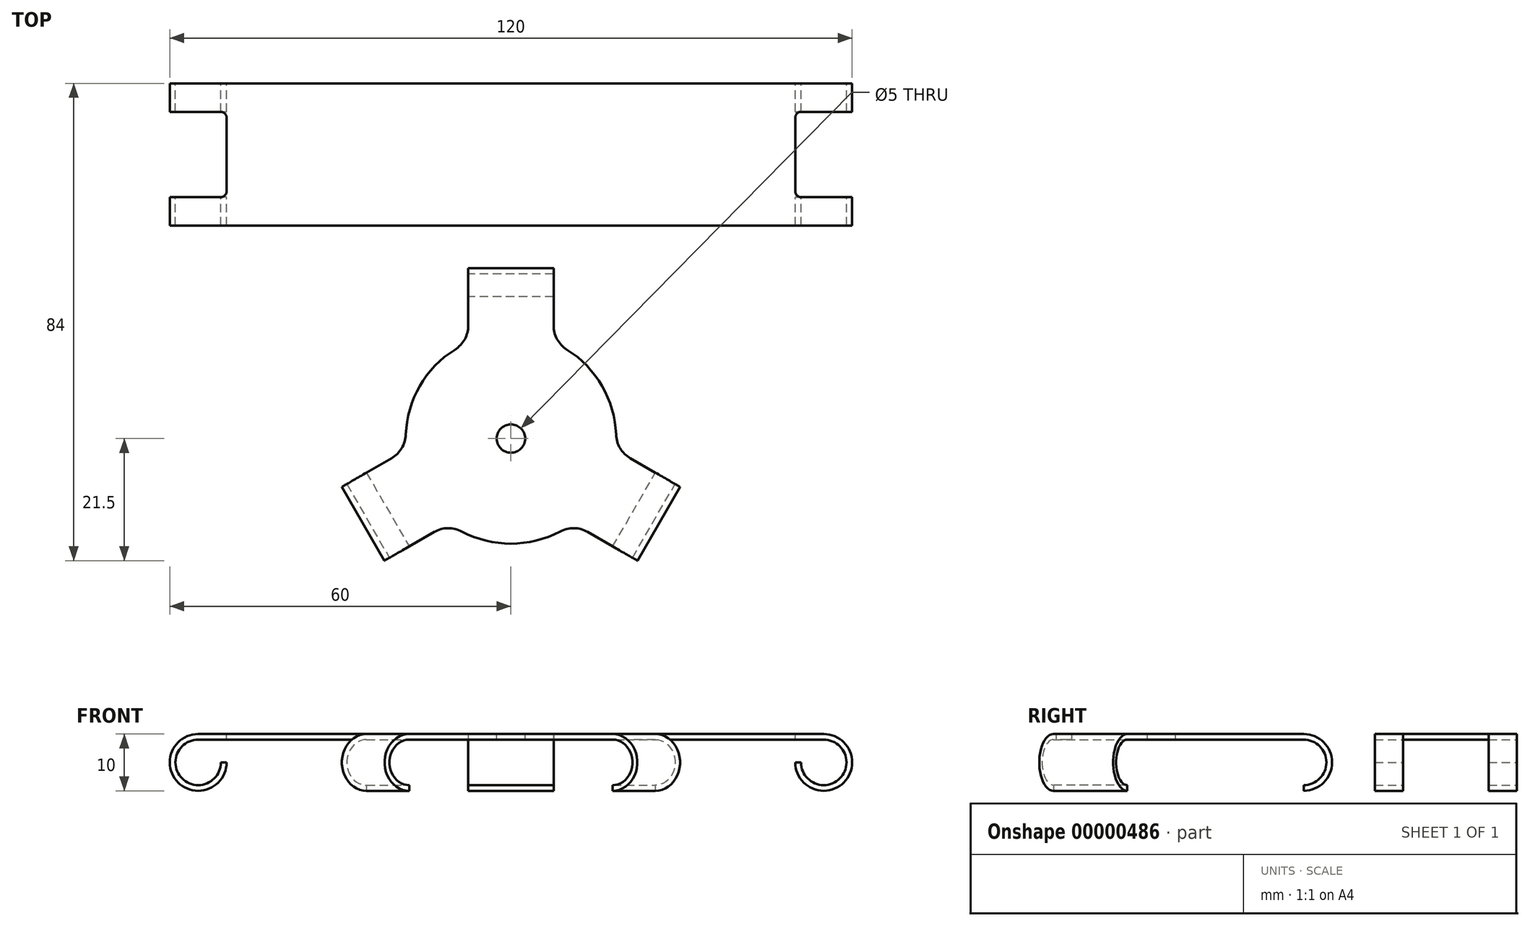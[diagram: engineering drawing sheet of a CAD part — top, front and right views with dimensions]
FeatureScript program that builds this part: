
annotation { "Feature Type Name" : "Feature", "Feature Type Description" : "" }
export const myFeature = defineFeature(function(context is Context, id is Id, definition is map)
    precondition{}
    {
        {
            var Q0;
            Q0     = qCreatedBy(makeId("Front.planeOp"), FACE);
            var sketch = newSketch(context, id + "F0", { "sketchPlane" : qUnion([Q0])});
            skLineSegment(sketch, "E0", {"start": v(-55, 0) * mm, "end": v(55, 0) * mm});
            skArc(sketch, "E1", {"start": v(-55, 0) * mm, "mid": v(-58.54, -8.54) * mm, "end": v(-50, -5) * mm});
            skArc(sketch, "E2", {"start": v(55, 0) * mm, "mid": v(58.54, -8.54) * mm, "end": v(50, -5) * mm});
            skArc(sketch, "E3.0", {"start": v(55, -1) * mm, "mid": v(57.83, -7.83) * mm, "end": v(51, -5) * mm});
            skLineSegment(sketch, "E3.1", {"start": v(-55, -1) * mm, "end": v(55, -1) * mm});
            skArc(sketch, "E3.2", {"start": v(-55, -1) * mm, "mid": v(-57.83, -7.83) * mm, "end": v(-51, -5) * mm});
            skLineSegment(sketch, "E4", {"start": v(-51, -5) * mm, "end": v(-50, -5) * mm});
            skLineSegment(sketch, "E5", {"start": v(51, -5) * mm, "end": v(50, -5) * mm});
            skSolve(sketch);
        }
        {
            var Q0;
            Q0=makeQuery(id+"F0.imprint","IMPRINT",FACE,{"disambiguationData":[TD([[makeQuery(id+"F0.imprint","IMPRINT",EDGE,{"derivedFrom":sQuery(id+"F0.wireOp",EDGE,"E0")}),-1.0]])]});
            extrude(context, id + "F1", {"entities" : qUnion([Q0]), "depth" : 25 * mm, "symmetric" : true});
        }
        {
            var Q0;
            Q0     = qCreatedBy(makeId("Top.planeOp"), FACE);
            var sketch = newSketch(context, id + "F2", { "sketchPlane" : qUnion([Q0])});
            skCircle(sketch, "E6", {"center": v(0, -50) * mm, "radius": 18.5 * mm});
            skLineSegment(sketch, "E7", {"start": v(0, -50) * mm, "end": v(0, -20) * mm, "construction": true});
            skLineSegment(sketch, "E8", {"start": v(0, -50) * mm, "end": v(25.98, -65) * mm, "construction": true});
            skLineSegment(sketch, "E9", {"start": v(0, -50) * mm, "end": v(-25.98, -65) * mm, "construction": true});
            skCircle(sketch, "E10", {"center": v(0, -50) * mm, "radius": 30 * mm, "construction": true});
            skLineSegment(sketch, "E11", {"start": v(-7.5, -20) * mm, "end": v(7.5, -20) * mm});
            skLineSegment(sketch, "E12", {"start": v(7.5, -20) * mm, "end": v(7.5, -45.67) * mm});
            skLineSegment(sketch, "E13", {"start": v(-7.5, -20) * mm, "end": v(-7.5, -45.67) * mm});
            skLineSegment(sketch, "E14", {"start": v(29.73, -58.5) * mm, "end": v(22.23, -71.5) * mm});
            skLineSegment(sketch, "E15", {"start": v(22.23, -71.5) * mm, "end": v(0, -58.66) * mm});
            skLineSegment(sketch, "E16", {"start": v(29.73, -58.5) * mm, "end": v(7.5, -45.67) * mm});
            skLineSegment(sketch, "E17", {"start": v(-29.73, -58.5) * mm, "end": v(-22.23, -71.5) * mm});
            skLineSegment(sketch, "E18", {"start": v(-22.23, -71.5) * mm, "end": v(0, -58.66) * mm});
            skLineSegment(sketch, "E19", {"start": v(-29.73, -58.5) * mm, "end": v(-7.5, -45.67) * mm});
            skSolve(sketch);
        }
        {
            var Q0;
            Q0=makeQuery(id+"F1.opExtrude","SWEPT_FACE",FACE,{"disambiguationData":[OSD([sQuery(id+"F0.wireOp",EDGE,"E0")])]});
            var sketch = newSketch(context, id + "F3", { "sketchPlane" : qUnion([Q0])});
            skLineSegment(sketch, "E20.rect.bottom", {"start": v(70, 7.5) * mm, "end": v(-70, 7.5) * mm});
            skLineSegment(sketch, "E20.rect.top", {"start": v(70, -7.5) * mm, "end": v(-70, -7.5) * mm});
            skLineSegment(sketch, "E20.rect.left", {"start": v(70, 7.5) * mm, "end": v(70, -7.5) * mm});
            skLineSegment(sketch, "E20.rect.right", {"start": v(-70, 7.5) * mm, "end": v(-70, -7.5) * mm});
            skPoint(sketch, "E20.rect.middle", {"position": v(0, 0) * mm});
            skLineSegment(sketch, "E21.bottom", {"start": v(-70, 7.5) * mm, "end": v(-50, 7.5) * mm});
            skLineSegment(sketch, "E21.top", {"start": v(-70, -7.5) * mm, "end": v(-50, -7.5) * mm});
            skLineSegment(sketch, "E21.right", {"start": v(-50, 7.5) * mm, "end": v(-50, -7.5) * mm});
            skLineSegment(sketch, "E22.bottom", {"start": v(70, 7.5) * mm, "end": v(50, 7.5) * mm});
            skLineSegment(sketch, "E22.top", {"start": v(70, -7.5) * mm, "end": v(50, -7.5) * mm});
            skLineSegment(sketch, "E22.right", {"start": v(50, 7.5) * mm, "end": v(50, -7.5) * mm});
            skSolve(sketch);
        }
        {
            var Q0;
            {var subQ5=sQuery(id+"F3.wireOp",EDGE,"E20.rect.right");Q0=makeQuery(id+"F3.imprint","IMPRINT",FACE,{"disambiguationData":[TD([[makeQuery(id+"F3.imprint","IMPRINT",EDGE,{"derivedFrom":subQ5}),1.0]])]});}
            var Q1;
            {var subQ5=sQuery(id+"F3.wireOp",EDGE,"E21.right");Q1=makeQuery(id+"F3.imprint","IMPRINT",FACE,{"disambiguationData":[TD([[makeQuery(id+"F3.imprint","IMPRINT",EDGE,{"derivedFrom":subQ5}),-1.0]])]});}
            var Q2;
            {var subQ5=sQuery(id+"F3.wireOp",EDGE,"E22.right");Q2=makeQuery(id+"F3.imprint","IMPRINT",FACE,{"disambiguationData":[TD([[makeQuery(id+"F3.imprint","IMPRINT",EDGE,{"derivedFrom":subQ5}),1.0]])]});}
            var Q3;
            {var subQ5=sQuery(id+"F3.wireOp",EDGE,"E20.rect.left");Q3=makeQuery(id+"F3.imprint","IMPRINT",FACE,{"disambiguationData":[TD([[makeQuery(id+"F3.imprint","IMPRINT",EDGE,{"derivedFrom":subQ5}),-1.0]])]});}
            extrude(context, id + "F4", {"entities" : qUnion([Q0, Q1, Q2, Q3]), "operationType" : NewBodyOperationType.REMOVE, "oppositeDirection" : true, "depth" : 25 * mm});
        }
        {
            var Q0;
            {var subQ0=sQuery(id+"F2.wireOp",EDGE,"E13");var subQ1=sQuery(id+"F2.wireOp",EDGE,"E6");var subQ2=makeQuery(id+"F2.imprint","INTERSECT",VERTEX,{"derivedFrom":[subQ1,subQ0]});var subQ3=sQuery(id+"F2.wireOp",EDGE,"E11");var subQ4=sQuery(id+"F2.wireOp",EDGE,"E12");var subQ5=makeQuery(id+"F2.imprint","INTERSECT",VERTEX,{"derivedFrom":[subQ1,subQ4]});var subQ6=makeQuery(id+"F2.imprint","IMPRINT",EDGE,{"disambiguationData":[TD([[subQ2,1.0]])],"derivedFrom":subQ1});var subQ12=sQuery(id+"F2.wireOp",EDGE,"E18");var subQ13=makeQuery(id+"F2.imprint","INTERSECT",VERTEX,{"derivedFrom":[subQ1,subQ12]});var subQ14=sQuery(id+"F2.wireOp",EDGE,"E17");var subQ23=sQuery(id+"F2.wireOp",EDGE,"E14");Q0=qUnion([makeQuery(id+"F2.imprint","IMPRINT",FACE,{"disambiguationData":[TD([[makeQuery(id+"F2.imprint","IMPRINT",EDGE,{"derivedFrom":subQ3}),-1.0]])]}),makeQuery(id+"F2.imprint","IMPRINT",FACE,{"disambiguationData":[TD([[makeQuery(id+"F2.imprint","IMPRINT",EDGE,{"disambiguationData":[TD([[subQ2,-1.0]])],"derivedFrom":subQ1}),1.0]])]}),makeQuery(id+"F2.imprint","IMPRINT",FACE,{"disambiguationData":[TD([[makeQuery(id+"F2.imprint","IMPRINT",EDGE,{"derivedFrom":subQ14}),1.0]])]}),makeQuery(id+"F2.imprint","IMPRINT",FACE,{"disambiguationData":[TD([[makeQuery(id+"F2.imprint","IMPRINT",EDGE,{"disambiguationData":[TD([[subQ13,-1.0]])],"derivedFrom":subQ1}),1.0]])]}),makeQuery(id+"F2.imprint","IMPRINT",FACE,{"disambiguationData":[TD([[makeQuery(id+"F2.imprint","IMPRINT",EDGE,{"derivedFrom":subQ23}),-1.0]])]}),makeQuery(id+"F2.imprint","IMPRINT",FACE,{"disambiguationData":[TD([[makeQuery(id+"F2.imprint","IMPRINT",EDGE,{"disambiguationData":[TD([[subQ5,1.0]])],"derivedFrom":subQ1}),1.0]])]}),makeQuery(id+"F2.imprint","IMPRINT",FACE,{"disambiguationData":[TD([[subQ6,1.0]])]})]);}
            extrude(context, id + "F5", {"entities" : qUnion([Q0]), "oppositeDirection" : true, "depth" : 10 * mm});
        }
        {
            var Q0;
            Q0=makeQuery(id+"F5.opExtrude","CAP_EDGE",EDGE,{"disambiguationData":[OSD([sQuery(id+"F2.wireOp",EDGE,"E17")])],"isStart":true});
            var Q1;
            Q1=makeQuery(id+"F5.opExtrude","CAP_EDGE",EDGE,{"disambiguationData":[OSD([sQuery(id+"F2.wireOp",EDGE,"E17")])],"isStart":false});
            var Q2;
            Q2=makeQuery(id+"F5.opExtrude","CAP_EDGE",EDGE,{"disambiguationData":[OSD([sQuery(id+"F2.wireOp",EDGE,"E14")])],"isStart":true});
            var Q3;
            Q3=makeQuery(id+"F5.opExtrude","CAP_EDGE",EDGE,{"disambiguationData":[OSD([sQuery(id+"F2.wireOp",EDGE,"E14")])],"isStart":false});
            var Q4;
            Q4=makeQuery(id+"F5.opExtrude","CAP_EDGE",EDGE,{"disambiguationData":[OSD([sQuery(id+"F2.wireOp",EDGE,"E11")])],"isStart":true});
            var Q5;
            Q5=makeQuery(id+"F5.opExtrude","CAP_EDGE",EDGE,{"disambiguationData":[OSD([sQuery(id+"F2.wireOp",EDGE,"E11")])],"isStart":false});
            fillet(context, id + "F6", {"entities" : qUnion([Q0, Q1, Q2, Q3, Q4, Q5]), "radius" : 5 * mm, "tangentPropagation" : true, "allowEdgeOverflow" : false});
        }
        {
            var Q0;
            Q0=makeQuery(id+"F5.opExtrude","CAP_FACE",FACE,{"disambiguationData":[OSD([sQuery(id+"F2.wireOp",EDGE,"E6"),sQuery(id+"F2.wireOp",EDGE,"E11"),sQuery(id+"F2.wireOp",EDGE,"E12"),sQuery(id+"F2.wireOp",EDGE,"E13"),sQuery(id+"F2.wireOp",EDGE,"E14"),sQuery(id+"F2.wireOp",EDGE,"E15"),sQuery(id+"F2.wireOp",EDGE,"E16"),sQuery(id+"F2.wireOp",EDGE,"E17"),sQuery(id+"F2.wireOp",EDGE,"E18"),sQuery(id+"F2.wireOp",EDGE,"E19")])],"isStart":false});
            extrude(context, id + "F7", {"entities" : qUnion([Q0]), "operationType" : NewBodyOperationType.REMOVE, "oppositeDirection" : true, "depth" : 3 * mm});
        }
        {
            var Q0;
            {var subQ0=sQuery(id+"F2.wireOp",EDGE,"E6");Q0=makeQuery(id+"F5.opExtrude","SWEPT_FACE",FACE,{"disambiguationData":[OSD([subQ0]),TDD([makeQuery(id+"F2.imprint","IMPRINT",EDGE,{"disambiguationData":[TD([[makeQuery(id+"F2.imprint","INTERSECT",VERTEX,{"derivedFrom":[subQ0,sQuery(id+"F2.wireOp",EDGE,"E12")]}),1.0]])],"derivedFrom":subQ0})])]});}
            var Q1;
            {var subQ0=sQuery(id+"F2.wireOp",EDGE,"E6");Q1=makeQuery(id+"F5.opExtrude","SWEPT_FACE",FACE,{"disambiguationData":[OSD([subQ0]),TDD([makeQuery(id+"F2.imprint","IMPRINT",EDGE,{"disambiguationData":[TD([[makeQuery(id+"F2.imprint","INTERSECT",VERTEX,{"derivedFrom":[subQ0,sQuery(id+"F2.wireOp",EDGE,"E18")]}),-1.0]])],"derivedFrom":subQ0})])]});}
            var Q2;
            Q2=makeQuery(id+"F5.opExtrude","SWEPT_FACE",FACE,{"disambiguationData":[OSD([sQuery(id+"F2.wireOp",EDGE,"E18")])]});
            var Q3;
            Q3=makeQuery(id+"F5.opExtrude","SWEPT_FACE",FACE,{"disambiguationData":[OSD([sQuery(id+"F2.wireOp",EDGE,"E12")])]});
            var Q4;
            Q4=makeQuery(id+"F5.opExtrude","SWEPT_FACE",FACE,{"disambiguationData":[OSD([sQuery(id+"F2.wireOp",EDGE,"E16")])]});
            var Q5;
            Q5=makeQuery(id+"F7.boolean.opBoolean","COPY",FACE,{"derivedFrom":makeQuery(id+"F7.opExtrude","CAP_FACE",FACE,{"disambiguationData":[OSD([sQuery(id+"F2.wireOp",EDGE,"E6"),sQuery(id+"F2.wireOp",EDGE,"E11"),sQuery(id+"F2.wireOp",EDGE,"E12"),sQuery(id+"F2.wireOp",EDGE,"E13"),sQuery(id+"F2.wireOp",EDGE,"E14"),sQuery(id+"F2.wireOp",EDGE,"E15"),sQuery(id+"F2.wireOp",EDGE,"E16"),sQuery(id+"F2.wireOp",EDGE,"E17"),sQuery(id+"F2.wireOp",EDGE,"E18"),sQuery(id+"F2.wireOp",EDGE,"E19")])],"isStart":false})});
            var Q6;
            Q6=makeQuery(id+"F5.opExtrude","SWEPT_FACE",FACE,{"disambiguationData":[OSD([sQuery(id+"F2.wireOp",EDGE,"E15")])]});
            var Q7;
            Q7=makeQuery(id+"F5.opExtrude","SWEPT_FACE",FACE,{"disambiguationData":[OSD([sQuery(id+"F2.wireOp",EDGE,"E19")])]});
            var Q8;
            {var subQ0=sQuery(id+"F2.wireOp",EDGE,"E6");Q8=makeQuery(id+"F5.opExtrude","SWEPT_FACE",FACE,{"disambiguationData":[OSD([subQ0]),TDD([makeQuery(id+"F2.imprint","IMPRINT",EDGE,{"disambiguationData":[TD([[makeQuery(id+"F2.imprint","INTERSECT",VERTEX,{"derivedFrom":[subQ0,sQuery(id+"F2.wireOp",EDGE,"E13")]}),-1.0]])],"derivedFrom":subQ0})])]});}
            var Q9;
            Q9=makeQuery(id+"F5.opExtrude","SWEPT_FACE",FACE,{"disambiguationData":[OSD([sQuery(id+"F2.wireOp",EDGE,"E13")])]});
            var Q10;
            {var subQ0=sQuery(id+"F2.wireOp",EDGE,"E6");var subQ1=sQuery(id+"F2.wireOp",EDGE,"E11");var subQ2=sQuery(id+"F2.wireOp",EDGE,"E12");var subQ3=sQuery(id+"F2.wireOp",EDGE,"E13");var subQ4=sQuery(id+"F2.wireOp",EDGE,"E14");var subQ5=sQuery(id+"F2.wireOp",EDGE,"E15");var subQ6=sQuery(id+"F2.wireOp",EDGE,"E16");var subQ7=sQuery(id+"F2.wireOp",EDGE,"E17");var subQ8=sQuery(id+"F2.wireOp",EDGE,"E18");var subQ9=sQuery(id+"F2.wireOp",EDGE,"E19");Q10=makeQuery(id+"F7.boolean.opBoolean","COPY",FACE,{"derivedFrom":makeQuery(id+"F7.opExtrude","SWEPT_FACE",FACE,{"disambiguationData":[OSD([subQ0,subQ1,subQ2,subQ3,subQ4,subQ5,subQ6,subQ7,subQ8,subQ9]),TDD([makeQuery(id+"F6.opFillet","BLEND_EDGE",EDGE,{"blendedFrom":[makeQuery(id+"F5.opExtrude","CAP_EDGE",EDGE,{"disambiguationData":[OSD([subQ4])],"isStart":false}),makeQuery(id+"F5.opExtrude","CAP_FACE",FACE,{"disambiguationData":[OSD([subQ0,subQ1,subQ2,subQ3,subQ4,subQ5,subQ6,subQ7,subQ8,subQ9])],"isStart":false})],"blendedInto":[makeQuery(id+"F5.opExtrude","CAP_FACE",FACE,{"disambiguationData":[OSD([subQ0,subQ1,subQ2,subQ3,subQ4,subQ5,subQ6,subQ7,subQ8,subQ9])],"isStart":false})]})])]})});}
            var Q11;
            {var subQ0=sQuery(id+"F2.wireOp",EDGE,"E6");var subQ1=sQuery(id+"F2.wireOp",EDGE,"E11");var subQ2=sQuery(id+"F2.wireOp",EDGE,"E12");var subQ3=sQuery(id+"F2.wireOp",EDGE,"E13");var subQ4=sQuery(id+"F2.wireOp",EDGE,"E14");var subQ5=sQuery(id+"F2.wireOp",EDGE,"E15");var subQ6=sQuery(id+"F2.wireOp",EDGE,"E16");var subQ7=sQuery(id+"F2.wireOp",EDGE,"E17");var subQ8=sQuery(id+"F2.wireOp",EDGE,"E18");var subQ9=sQuery(id+"F2.wireOp",EDGE,"E19");Q11=makeQuery(id+"F7.boolean.opBoolean","COPY",FACE,{"derivedFrom":makeQuery(id+"F7.opExtrude","SWEPT_FACE",FACE,{"disambiguationData":[OSD([subQ0,subQ1,subQ2,subQ3,subQ4,subQ5,subQ6,subQ7,subQ8,subQ9]),TDD([makeQuery(id+"F6.opFillet","BLEND_EDGE",EDGE,{"blendedFrom":[makeQuery(id+"F5.opExtrude","CAP_EDGE",EDGE,{"disambiguationData":[OSD([subQ1])],"isStart":false}),makeQuery(id+"F5.opExtrude","CAP_FACE",FACE,{"disambiguationData":[OSD([subQ0,subQ1,subQ2,subQ3,subQ4,subQ5,subQ6,subQ7,subQ8,subQ9])],"isStart":false})],"blendedInto":[makeQuery(id+"F5.opExtrude","CAP_FACE",FACE,{"disambiguationData":[OSD([subQ0,subQ1,subQ2,subQ3,subQ4,subQ5,subQ6,subQ7,subQ8,subQ9])],"isStart":false})]})])]})});}
            var Q12;
            {var subQ0=sQuery(id+"F2.wireOp",EDGE,"E6");var subQ1=sQuery(id+"F2.wireOp",EDGE,"E11");var subQ2=sQuery(id+"F2.wireOp",EDGE,"E12");var subQ3=sQuery(id+"F2.wireOp",EDGE,"E13");var subQ4=sQuery(id+"F2.wireOp",EDGE,"E14");var subQ5=sQuery(id+"F2.wireOp",EDGE,"E15");var subQ6=sQuery(id+"F2.wireOp",EDGE,"E16");var subQ7=sQuery(id+"F2.wireOp",EDGE,"E17");var subQ8=sQuery(id+"F2.wireOp",EDGE,"E18");var subQ9=sQuery(id+"F2.wireOp",EDGE,"E19");Q12=makeQuery(id+"F7.boolean.opBoolean","COPY",FACE,{"derivedFrom":makeQuery(id+"F7.opExtrude","SWEPT_FACE",FACE,{"disambiguationData":[OSD([subQ0,subQ1,subQ2,subQ3,subQ4,subQ5,subQ6,subQ7,subQ8,subQ9]),TDD([makeQuery(id+"F6.opFillet","BLEND_EDGE",EDGE,{"blendedFrom":[makeQuery(id+"F5.opExtrude","CAP_EDGE",EDGE,{"disambiguationData":[OSD([subQ7])],"isStart":false}),makeQuery(id+"F5.opExtrude","CAP_FACE",FACE,{"disambiguationData":[OSD([subQ0,subQ1,subQ2,subQ3,subQ4,subQ5,subQ6,subQ7,subQ8,subQ9])],"isStart":false})],"blendedInto":[makeQuery(id+"F5.opExtrude","CAP_FACE",FACE,{"disambiguationData":[OSD([subQ0,subQ1,subQ2,subQ3,subQ4,subQ5,subQ6,subQ7,subQ8,subQ9])],"isStart":false})]})])]})});}
            shell(context, id + "F8", {"entities" : qUnion([Q0, Q1, Q2, Q3, Q4, Q5, Q6, Q7, Q8, Q9, Q10, Q11, Q12]), "thickness" : 1 * mm});
        }
        {
            var Q0;
            Q0=makeQuery(id+"F5.opExtrude","SWEPT_EDGE",EDGE,{"disambiguationData":[OSD([sQuery(id+"F2.wireOp",EDGE,"E6"),sQuery(id+"F2.wireOp",EDGE,"E13")])]});
            var Q1;
            Q1=makeQuery(id+"F5.opExtrude","SWEPT_EDGE",EDGE,{"disambiguationData":[OSD([sQuery(id+"F2.wireOp",EDGE,"E6"),sQuery(id+"F2.wireOp",EDGE,"E19")])]});
            var Q2;
            Q2=makeQuery(id+"F5.opExtrude","SWEPT_EDGE",EDGE,{"disambiguationData":[OSD([sQuery(id+"F2.wireOp",EDGE,"E6"),sQuery(id+"F2.wireOp",EDGE,"E16")])]});
            var Q3;
            Q3=makeQuery(id+"F5.opExtrude","SWEPT_EDGE",EDGE,{"disambiguationData":[OSD([sQuery(id+"F2.wireOp",EDGE,"E6"),sQuery(id+"F2.wireOp",EDGE,"E12")])]});
            var Q4;
            Q4=makeQuery(id+"F5.opExtrude","SWEPT_EDGE",EDGE,{"disambiguationData":[OSD([sQuery(id+"F2.wireOp",EDGE,"E6"),sQuery(id+"F2.wireOp",EDGE,"E18")])]});
            var Q5;
            Q5=makeQuery(id+"F5.opExtrude","SWEPT_EDGE",EDGE,{"disambiguationData":[OSD([sQuery(id+"F2.wireOp",EDGE,"E6"),sQuery(id+"F2.wireOp",EDGE,"E15")])]});
            fillet(context, id + "F9", {"entities" : qUnion([Q0, Q1, Q2, Q3, Q4, Q5]), "radius" : 5 * mm, "tangentPropagation" : true, "allowEdgeOverflow" : false});
        }
        {
            var Q0;
            Q0=makeQuery(id+"F4.boolean.opBoolean","COPY",EDGE,{"derivedFrom":makeQuery(id+"F4.opExtrude","SWEPT_EDGE",EDGE,{"disambiguationData":[OSD([sQuery(id+"F3.wireOp",EDGE,"E20.rect.bottom"),sQuery(id+"F3.wireOp",EDGE,"E22.bottom"),sQuery(id+"F3.wireOp",EDGE,"E22.right")])]})});
            var Q1;
            Q1=makeQuery(id+"F4.boolean.opBoolean","COPY",EDGE,{"derivedFrom":makeQuery(id+"F4.opExtrude","SWEPT_EDGE",EDGE,{"disambiguationData":[OSD([sQuery(id+"F3.wireOp",EDGE,"E20.rect.top"),sQuery(id+"F3.wireOp",EDGE,"E22.top"),sQuery(id+"F3.wireOp",EDGE,"E22.right")])]})});
            var Q2;
            Q2=makeQuery(id+"F4.boolean.opBoolean","COPY",EDGE,{"derivedFrom":makeQuery(id+"F4.opExtrude","SWEPT_EDGE",EDGE,{"disambiguationData":[OSD([sQuery(id+"F3.wireOp",EDGE,"E20.rect.bottom"),sQuery(id+"F3.wireOp",EDGE,"E21.bottom"),sQuery(id+"F3.wireOp",EDGE,"E21.right")])]})});
            var Q3;
            Q3=makeQuery(id+"F4.boolean.opBoolean","COPY",EDGE,{"derivedFrom":makeQuery(id+"F4.opExtrude","SWEPT_EDGE",EDGE,{"disambiguationData":[OSD([sQuery(id+"F3.wireOp",EDGE,"E20.rect.top"),sQuery(id+"F3.wireOp",EDGE,"E21.top"),sQuery(id+"F3.wireOp",EDGE,"E21.right")])]})});
            fillet(context, id + "F10", {"entities" : qUnion([Q0, Q1, Q2, Q3]), "radius" : 1 * mm, "tangentPropagation" : true, "allowEdgeOverflow" : false});
        }
        {
            var Q0;
            Q0=makeQuery(id+"F5.opExtrude","CAP_FACE",FACE,{"disambiguationData":[OSD([sQuery(id+"F2.wireOp",EDGE,"E6"),sQuery(id+"F2.wireOp",EDGE,"E11"),sQuery(id+"F2.wireOp",EDGE,"E12"),sQuery(id+"F2.wireOp",EDGE,"E13"),sQuery(id+"F2.wireOp",EDGE,"E14"),sQuery(id+"F2.wireOp",EDGE,"E15"),sQuery(id+"F2.wireOp",EDGE,"E16"),sQuery(id+"F2.wireOp",EDGE,"E17"),sQuery(id+"F2.wireOp",EDGE,"E18"),sQuery(id+"F2.wireOp",EDGE,"E19")])],"isStart":true});
            var sketch = newSketch(context, id + "F11", { "sketchPlane" : qUnion([Q0])});
            skCircle(sketch, "E23", {"center": v(0, -50) * mm, "radius": 2.5 * mm});
            skSolve(sketch);
        }
        {
            var Q0;
            Q0=makeQuery(id+"F11.imprint","IMPRINT",FACE,{"disambiguationData":[TD([[makeQuery(id+"F11.imprint","IMPRINT",EDGE,{"derivedFrom":sQuery(id+"F11.wireOp",EDGE,"E23")}),1.0]])]});
            extrude(context, id + "F12", {"entities" : qUnion([Q0]), "operationType" : NewBodyOperationType.REMOVE, "oppositeDirection" : true, "depth" : 25 * mm});
        }
    });
